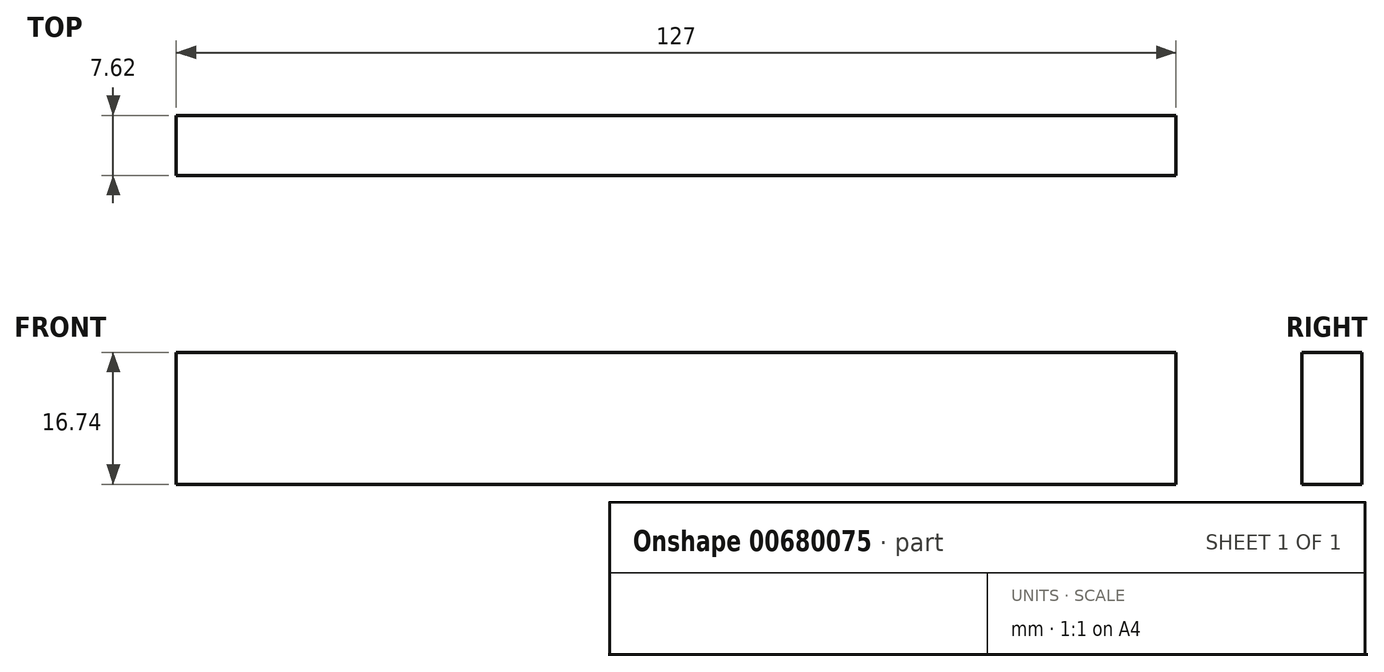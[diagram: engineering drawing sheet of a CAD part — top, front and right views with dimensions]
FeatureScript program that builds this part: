
annotation { "Feature Type Name" : "Feature", "Feature Type Description" : "" }
export const myFeature = defineFeature(function(context is Context, id is Id, definition is map)
    precondition{}
    {
        {
            var Q0;
            Q0=qCreatedBy(makeId("Front.planeOp"),FACE);
            var sketch = newSketch(context, id + "F0", { "sketchPlane" : qUnion([Q0])});
            skLineSegment(sketch, "E0.bottom", {"start": v(-63.5, 8.37) * mm, "end": v(63.5, 8.37) * mm});
            skLineSegment(sketch, "E0.top", {"start": v(-63.5, -8.37) * mm, "end": v(63.5, -8.37) * mm});
            skLineSegment(sketch, "E0.left", {"start": v(-63.5, 8.37) * mm, "end": v(-63.5, -8.37) * mm});
            skLineSegment(sketch, "E0.right", {"start": v(63.5, 8.37) * mm, "end": v(63.5, -8.37) * mm});
            skPoint(sketch, "E0.middle", {"position": v(0, 0) * mm});
            skSolve(sketch);
        }
        {
            var Q0;
            Q0=makeQuery(id+"F0.imprint","IMPRINT",FACE,{"disambiguationData":[TD([[makeQuery(id+"F0.imprint","IMPRINT",EDGE,{"derivedFrom":sQuery(id+"F0.wireOp",EDGE,"E0.bottom")}),-1.0]])]});
            extrude(context, id + "F1", {"entities" : qUnion([Q0]), "depth" : 7.62 * mm, "offsetDistance" : 25.4 * mm});
        }
    });
